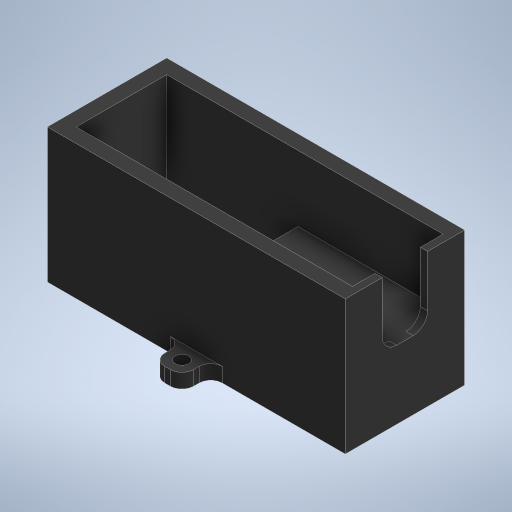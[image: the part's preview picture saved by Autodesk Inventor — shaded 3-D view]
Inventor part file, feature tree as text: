
AUTODESK INVENTOR PART (.ipt)
format: ipt  version: 2024 (Build 280153000, 153)  size: 313,856 bytes
history: native  units: in
note: dims shown in document units (in); Inventor stores cm internally (conversion verified against a paired STEP export)
features: extrude x5, sketch x5, fillet x2, plane x1, mirror x1, projected_geometry x1
ambient origin geometry x8: Origin, YZ Plane, XZ Plane, XY Plane, X Axis, Y Axis, Z Axis, Center Point
bodies: Solid1 (feature_tree)
feature tree (15):
  extrude  "Extrusion1"  Depth=0.47in
  sketch  "Sketch2"  dims[d2=1.1417in d3=1.6142in]
  plane  "Work Plane1"
  extrude  "Extrusion2"  Depth=1.1417in
  mirror  "Mirror1"
  extrude  "Extrusion3"  Depth=0.063in
  fillet  "Fillet1"  Radius=0.125in
  extrude  "Extrusion4"  Depth=0.125in
  fillet  "Fillet2"  Radius=0.7874in
  extrude  "Extrusion5"  Depth=0.125in TaperAngle=0.0deg
  sketch  "Sketch1"  dims[d0=1.2598in d1=0.47in]
  sketch  "Sketch3"  dims[d4=0.4724in d5=0.063in d7=0.125in]
  sketch  "Sketch4"  dims[d8=0.125in d9=0.125in d10=0.7874in d11=0.0in]
  sketch  "Sketch5"  dims[d12=-0.3937in d13=0.125in d14=0.0in d15=0.1969in d16=0.1969in d17=0.125in d18=0.0in d19=0.125in d20=0.125in d21=0.25in d22=0.125in d23=0.1181in d24=0.125in d25=0.0in d26=0.1in d27=0.1in d28=0.0in]
  projected_geometry  "Projected Loop1"
